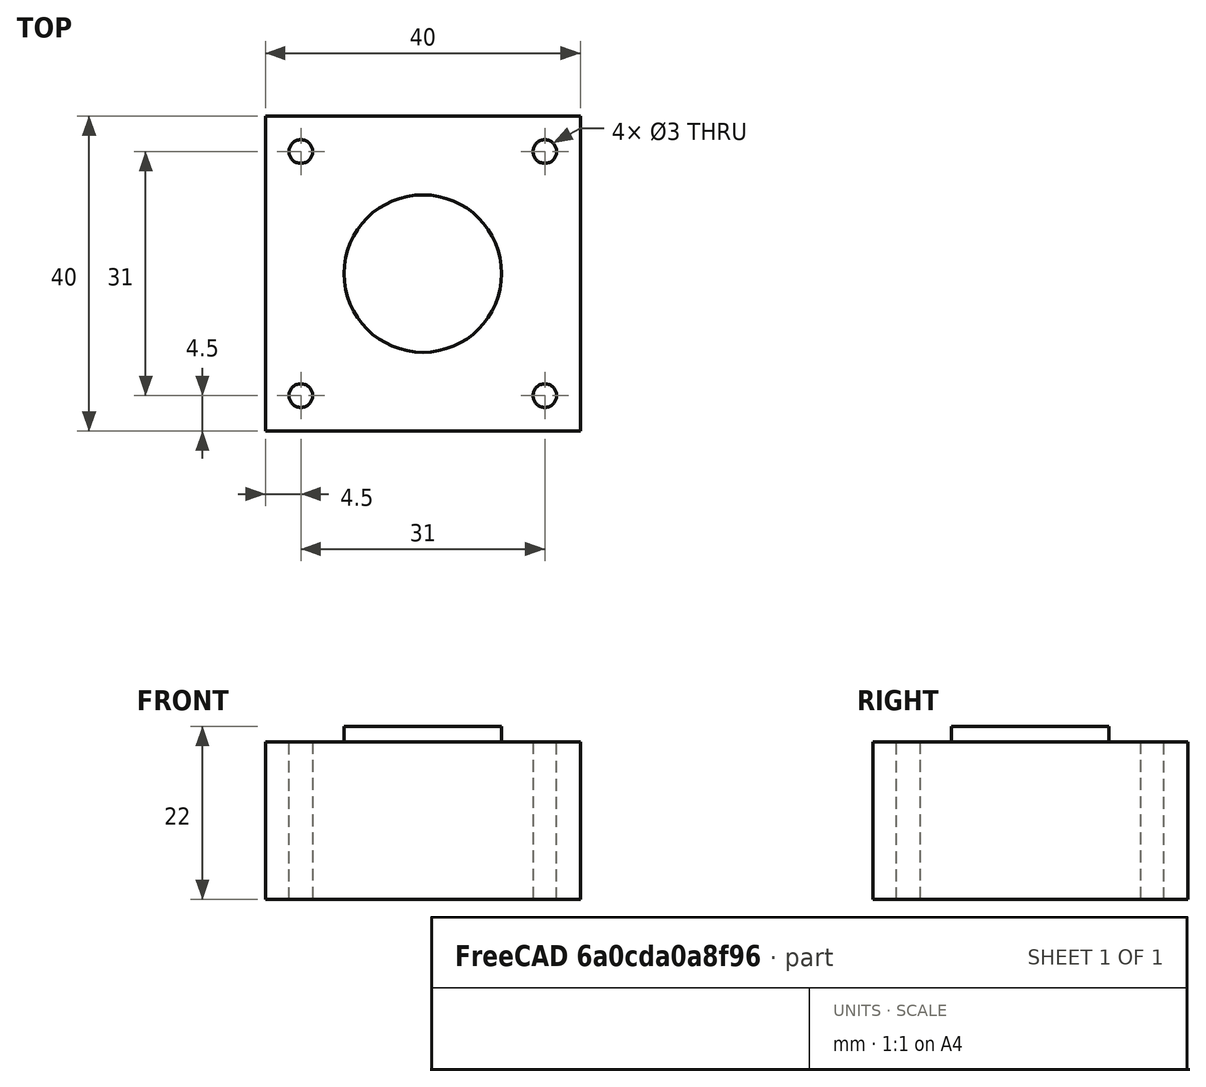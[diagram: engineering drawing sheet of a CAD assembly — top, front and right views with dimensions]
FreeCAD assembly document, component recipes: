
FREECAD ASSEMBLY — COMPONENT RECIPES ("Stepper")

This assembly document has 2 components, labeled P0..P1 below (a component is one placed body or linked part). 2 of them carry a construction recipe — the FreeCAD feature program that regenerates the part from scratch, quoted from this document or its linked companion documents; the rest are supplied as boundary geometry only. No exploded tour is included for this assembly.
COMPONENT P0 — recipe-attached ("Nema42_20", modeled in this document).
Construction recipe (the document's own serialized feature program — sketch geometry with constraints, then the solid features built on it; lengths are millimeters unless a unit is written):

FEATURE [Sketcher::SketchObject] Sketch018
  ArcFitTolerance = 1e-06
  AttachmentSupport = -> [XY_Plane005]
  FullyConstrained = true
  MakeInternals = false
  MapMode = 5
  sketch-geometry (5):
    g0: LineSegment StartX=20 StartY=-20 StartZ=0 EndX=20 EndY=20 EndZ=0
    g1: LineSegment StartX=20 StartY=20 StartZ=0 EndX=-20 EndY=20 EndZ=0
    g2: LineSegment StartX=-20 StartY=20 StartZ=0 EndX=-20 EndY=-20 EndZ=0
    g3: LineSegment StartX=-20 StartY=-20 StartZ=0 EndX=20 EndY=-20 EndZ=0
    g4: GeomPoint [constr] X=0 Y=0 Z=0
  constraints (12):
    c: Coincident(g0,g1)
    c: Coincident(g1,g2)
    c: Coincident(g2,g3)
    c: Coincident(g3,g0)
    c: Vertical(g0)
    c: Vertical(g2)
    c: Horizontal(g1)
    c: Horizontal(g3)
    c: Symmetric(g2,g0,g4)
    c: Coincident(g4,g-1)
    c: Distance(g-1,g1) = 20
    c: Distance(g-2,g2) = 20
FEATURE [PartDesign::Pad] Pad010
  Direction = (0,0,1)
  Length = 20
  Length2 = 10
  Profile = -> Sketch018
  ReferenceAxis = -> Sketch018 [N_Axis]
  Refine = true
  Suppressed = false
  Type = 0
FEATURE [Sketcher::SketchObject] Sketch019
  ArcFitTolerance = 1e-06
  AttachmentSupport = -> [Pad010]
  FullyConstrained = true
  MakeInternals = false
  MapMode = 5
  Placement = pos=(0,0,20) rot=(0,0,1;0rad)
  sketch-geometry (1):
    g0: Circle CenterX=0 CenterY=0 CenterZ=0 NormalX=0 NormalY=0 NormalZ=1 AngleXU=0 Radius=10
  constraints (2):
    c: Coincident(g0,g-1)
    c: Diameter(g0) = 20
FEATURE [PartDesign::Pad] Pad011
  BaseFeature = -> Pad010
  Direction = (0,0,1)
  Length = 2
  Length2 = 10
  Profile = -> Sketch019
  ReferenceAxis = -> Sketch019 [N_Axis]
  Refine = true
  Suppressed = false
  Type = 0
FEATURE [Sketcher::SketchObject] Sketch020
  ArcFitTolerance = 1e-06
  AttachmentSupport = -> [Pad011]
  FullyConstrained = true
  MakeInternals = false
  MapMode = 5
  Placement = pos=(0,0,20) rot=(0,0,1;0rad)
  sketch-geometry (1):
    g0: Circle CenterX=-15.5 CenterY=15.5 CenterZ=0 NormalX=0 NormalY=0 NormalZ=1 AngleXU=0 Radius=1.5
  constraints (3):
    c: Distance(g0,g-2) = 15.5
    c: DistanceY(g-1,g0) = 15.5
    c: Diameter(g0) = 3
FEATURE [PartDesign::Pocket] Pocket007
  BaseFeature = -> Pad011
  Direction = (0,0,-1)
  Length = 5
  Length2 = 5
  Profile = -> Sketch020
  ReferenceAxis = -> Sketch020 [N_Axis]
  Refine = true
  Suppressed = false
  Type = 1
FEATURE [PartDesign::PolarPattern] PolarPattern002
  Angle = 360
  Axis = -> Sketch020 [N_Axis]
  BaseFeature = -> Pocket007
  Mode = 0
  Occurrences = 4
  Offset = 120
  Originals = -> [Pocket007]
  Refine = true
  Suppressed = false
  TransformMode = 0
FEATURE [PartDesign::Body] Body005  label="Nema42_20"
  AllowCompound = false
  Group = -> [Sketch018,Pad010,Sketch019,Pad011,Sketch020,Pocket007,PolarPattern002]
  Origin = -> Origin005
  Placement = pos=(0,0,0) rot=(0,0,1;4.71239rad)
  Tip = -> PolarPattern002
COMPONENT P1 — recipe-attached ("GT2_Second_Min", a linked part whose construction recipe lives in a companion FreeCAD document of the same project; that document's serialized recipe follows).
Construction recipe (the companion document, serialized — sketch geometry with constraints, then the solid features built on it; lengths are millimeters unless a unit is written):

FCSTD DOCUMENT  (FreeCAD 1.0R39319 (Git))
Label: GT2_20
License: All rights reserved
LicenseURL: https://en.wikipedia.org/wiki/All_rights_reserved
objects: Sketcher::SketchObject×3, PartDesign::Pad×3, PartDesign::Body×1
note: 16 computed .brp shape members not serialized (recipe doc carries the construction recipe); baked Part::Feature solids carry a one-line shape summary decoded from their .brp

FEATURE [Sketcher::SketchObject] SketchGear
  ArcFitTolerance = 1e-06
  FullyConstrained = false
  MakeInternals = false
  MapMode = 5
  Placement = pos=(0,0,7.5) rot=(0,0,1;0rad)
  sketch-geometry (121):
    g0: ArcOfCircle CenterX=5.9622 CenterY=-0.75 CenterZ=0 NormalX=0 NormalY=0 NormalZ=1 AngleXU=8.1e-15 Radius=0.15 StartAngle=0 EndAngle=1.5708
    g1: ArcOfCircle CenterX=6.30816 CenterY=0.82798 CenterZ=0 NormalX=0 NormalY=0 NormalZ=-1 AngleXU=-1.3331 Radius=1.46929 StartAngle=0 EndAngle=0.255762
    g2: ArcOfCircle CenterX=5.92156 CenterY=0 CenterZ=0 NormalX=0 NormalY=0 NormalZ=-1 AngleXU=-0.984764 Radius=0.559359 StartAngle=0 EndAngle=1.96953
    g3: ArcOfCircle CenterX=6.30816 CenterY=-0.82798 CenterZ=0 NormalX=0 NormalY=0 NormalZ=-1 AngleXU=1.07734 Radius=1.46929 StartAngle=0 EndAngle=0.255762
    g4: ArcOfCircle CenterX=5.9622 CenterY=0.75 CenterZ=0 NormalX=0 NormalY=0 NormalZ=1 AngleXU=-1.5708 Radius=0.15 StartAngle=0 EndAngle=1.5708
    g5: LineSegment StartX=6.1122 StartY=0.75 StartZ=0 EndX=6.04481 EndY=1.17548 EndZ=0
    g6: ArcOfCircle CenterX=5.90215 CenterY=1.12913 CenterZ=0 NormalX=0 NormalY=0 NormalZ=1 AngleXU=0.314159 Radius=0.15 StartAngle=0 EndAngle=1.5708
    g7: ArcOfCircle CenterX=5.74356 CenterY=2.73679 CenterZ=0 NormalX=0 NormalY=0 NormalZ=-1 AngleXU=-1.64726 Radius=1.46929 StartAngle=0 EndAngle=0.255762
    g8: ArcOfCircle CenterX=5.63174 CenterY=1.82986 CenterZ=0 NormalX=0 NormalY=0 NormalZ=-1 AngleXU=-1.29892 Radius=0.559359 StartAngle=0 EndAngle=1.96953
    g9: ArcOfCircle CenterX=6.25528 CenterY=1.16187 CenterZ=0 NormalX=0 NormalY=0 NormalZ=-1 AngleXU=0.763178 Radius=1.46929 StartAngle=0 EndAngle=0.255762
    g10: ArcOfCircle CenterX=5.43862 CenterY=2.55571 CenterZ=0 NormalX=0 NormalY=0 NormalZ=1 AngleXU=-1.25664 Radius=0.15 StartAngle=0 EndAngle=1.5708
    g11: LineSegment StartX=5.58128 StartY=2.60207 StartZ=0 EndX=5.38571 EndY=2.9859 EndZ=0
    g12: ArcOfCircle CenterX=5.26436 CenterY=2.89773 CenterZ=0 NormalX=0 NormalY=0 NormalZ=1 AngleXU=0.628319 Radius=0.15 StartAngle=0 EndAngle=1.5708
    g13: ArcOfCircle CenterX=4.61674 CenterY=4.3777 CenterZ=0 NormalX=0 NormalY=0 NormalZ=-1 AngleXU=-1.96142 Radius=1.46929 StartAngle=0 EndAngle=0.255762
    g14: ArcOfCircle CenterX=4.79064 CenterY=3.4806 CenterZ=0 NormalX=0 NormalY=0 NormalZ=-1 AngleXU=-1.61308 Radius=0.559359 StartAngle=0 EndAngle=1.96953
    g15: ArcOfCircle CenterX=5.59009 CenterY=3.038 CenterZ=0 NormalX=0 NormalY=0 NormalZ=-1 AngleXU=0.449019 Radius=1.46929 StartAngle=0 EndAngle=0.255762
    g16: ArcOfCircle CenterX=4.38268 CenterY=4.11125 CenterZ=0 NormalX=0 NormalY=0 NormalZ=1 AngleXU=-0.942478 Radius=0.15 StartAngle=0 EndAngle=1.5708
    g17: LineSegment StartX=4.50403 StartY=4.19942 StartZ=0 EndX=4.19942 EndY=4.50403 EndZ=0
    g18: ArcOfCircle CenterX=4.11125 CenterY=4.38268 CenterZ=0 NormalX=0 NormalY=0 NormalZ=1 AngleXU=0.942478 Radius=0.15 StartAngle=0 EndAngle=1.5708
    g19: ArcOfCircle CenterX=3.038 CenterY=5.59009 CenterZ=0 NormalX=0 NormalY=0 NormalZ=-1 AngleXU=-2.27558 Radius=1.46929 StartAngle=0 EndAngle=0.255762
    g20: ArcOfCircle CenterX=3.4806 CenterY=4.79064 CenterZ=0 NormalX=0 NormalY=0 NormalZ=-1 AngleXU=-1.92724 Radius=0.559359 StartAngle=0 EndAngle=1.96953
    g21: ArcOfCircle CenterX=4.3777 CenterY=4.61674 CenterZ=0 NormalX=0 NormalY=0 NormalZ=-1 AngleXU=0.13486 Radius=1.46929 StartAngle=0 EndAngle=0.255762
    g22: ArcOfCircle CenterX=2.89773 CenterY=5.26436 CenterZ=0 NormalX=0 NormalY=0 NormalZ=1 AngleXU=-0.628319 Radius=0.15 StartAngle=0 EndAngle=1.5708
    g23: LineSegment StartX=2.9859 StartY=5.38571 StartZ=0 EndX=2.60207 EndY=5.58128 EndZ=0
    g24: ArcOfCircle CenterX=2.55571 CenterY=5.43862 CenterZ=0 NormalX=0 NormalY=0 NormalZ=1 AngleXU=1.25664 Radius=0.15 StartAngle=0 EndAngle=1.5708
    g25: ArcOfCircle CenterX=1.16187 CenterY=6.25528 CenterZ=0 NormalX=0 NormalY=0 NormalZ=-1 AngleXU=-2.58974 Radius=1.46929 StartAngle=0 EndAngle=0.255762
    g26: ArcOfCircle CenterX=1.82986 CenterY=5.63174 CenterZ=0 NormalX=0 NormalY=0 NormalZ=-1 AngleXU=-2.2414 Radius=0.559359 StartAngle=0 EndAngle=1.96953
    g27: ArcOfCircle CenterX=2.73679 CenterY=5.74356 CenterZ=0 NormalX=0 NormalY=0 NormalZ=-1 AngleXU=-0.1793 Radius=1.46929 StartAngle=0 EndAngle=0.255762
    g28: ArcOfCircle CenterX=1.12913 CenterY=5.90215 CenterZ=0 NormalX=0 NormalY=0 NormalZ=1 AngleXU=-0.314159 Radius=0.15 StartAngle=0 EndAngle=1.5708
    g29: LineSegment StartX=1.17548 StartY=6.04481 StartZ=0 EndX=0.75 EndY=6.1122 EndZ=0
    g30: ArcOfCircle CenterX=0.75 CenterY=5.9622 CenterZ=0 NormalX=0 NormalY=0 NormalZ=1 AngleXU=1.5708 Radius=0.15 StartAngle=0 EndAngle=1.5708
    g31: ArcOfCircle CenterX=-0.82798 CenterY=6.30816 CenterZ=0 NormalX=0 NormalY=0 NormalZ=-1 AngleXU=-2.9039 Radius=1.46929 StartAngle=0 EndAngle=0.255762
    g32: ArcOfCircle CenterX=4e-16 CenterY=5.92156 CenterZ=0 NormalX=0 NormalY=0 NormalZ=-1 AngleXU=-2.55556 Radius=0.559359 StartAngle=0 EndAngle=1.96953
    g33: ArcOfCircle CenterX=0.82798 CenterY=6.30816 CenterZ=0 NormalX=0 NormalY=0 NormalZ=-1 AngleXU=-0.493459 Radius=1.46929 StartAngle=0 EndAngle=0.255762
    g34: ArcOfCircle CenterX=-0.75 CenterY=5.9622 CenterZ=0 NormalX=0 NormalY=0 NormalZ=1 AngleXU=5.9e-15 Radius=0.15 StartAngle=0 EndAngle=1.5708
    g35: LineSegment StartX=-0.75 StartY=6.1122 StartZ=0 EndX=-1.17548 EndY=6.04481 EndZ=0
    g36: ArcOfCircle CenterX=-1.12913 CenterY=5.90215 CenterZ=0 NormalX=0 NormalY=0 NormalZ=1 AngleXU=1.88496 Radius=0.15 StartAngle=0 EndAngle=1.5708
    g37: ArcOfCircle CenterX=-2.73679 CenterY=5.74356 CenterZ=0 NormalX=0 NormalY=0 NormalZ=-1 AngleXU=3.06513 Radius=1.46929 StartAngle=0 EndAngle=0.255762
    g38: ArcOfCircle CenterX=-1.82986 CenterY=5.63174 CenterZ=0 NormalX=0 NormalY=0 NormalZ=-1 AngleXU=-2.86972 Radius=0.559359 StartAngle=0 EndAngle=1.96953
    g39: ArcOfCircle CenterX=-1.16187 CenterY=6.25528 CenterZ=0 NormalX=0 NormalY=0 NormalZ=-1 AngleXU=-0.807618 Radius=1.46929 StartAngle=0 EndAngle=0.255762
    g40: ArcOfCircle CenterX=-2.55571 CenterY=5.43862 CenterZ=0 NormalX=0 NormalY=0 NormalZ=1 AngleXU=0.314159 Radius=0.15 StartAngle=0 EndAngle=1.5708
    g41: LineSegment StartX=-2.60207 StartY=5.58128 StartZ=0 EndX=-2.9859 EndY=5.38571 EndZ=0
    g42: ArcOfCircle CenterX=-2.89773 CenterY=5.26436 CenterZ=0 NormalX=0 NormalY=0 NormalZ=1 AngleXU=2.19911 Radius=0.15 StartAngle=0 EndAngle=1.5708
    g43: ArcOfCircle CenterX=-4.3777 CenterY=4.61674 CenterZ=0 NormalX=0 NormalY=0 NormalZ=-1 AngleXU=2.75097 Radius=1.46929 StartAngle=0 EndAngle=0.255762
    g44: ArcOfCircle CenterX=-3.4806 CenterY=4.79064 CenterZ=0 NormalX=0 NormalY=0 NormalZ=-1 AngleXU=3.09931 Radius=0.559359 StartAngle=0 EndAngle=1.96953
    g45: ArcOfCircle CenterX=-3.038 CenterY=5.59009 CenterZ=0 NormalX=0 NormalY=0 NormalZ=-1 AngleXU=-1.12178 Radius=1.46929 StartAngle=0 EndAngle=0.255762
    g46: ArcOfCircle CenterX=-4.11125 CenterY=4.38268 CenterZ=0 NormalX=0 NormalY=0 NormalZ=1 AngleXU=0.628319 Radius=0.15 StartAngle=0 EndAngle=1.5708
    g47: LineSegment StartX=-4.19942 StartY=4.50403 StartZ=0 EndX=-4.50403 EndY=4.19942 EndZ=0
    g48: ArcOfCircle CenterX=-4.38268 CenterY=4.11125 CenterZ=0 NormalX=0 NormalY=0 NormalZ=1 AngleXU=2.51327 Radius=0.15 StartAngle=0 EndAngle=1.5708
    g49: ArcOfCircle CenterX=-5.59009 CenterY=3.038 CenterZ=0 NormalX=0 NormalY=0 NormalZ=-1 AngleXU=2.43681 Radius=1.46929 StartAngle=0 EndAngle=0.255762
    g50: ArcOfCircle CenterX=-4.79064 CenterY=3.4806 CenterZ=0 NormalX=0 NormalY=0 NormalZ=-1 AngleXU=2.78515 Radius=0.559359 StartAngle=0 EndAngle=1.96953
    g51: ArcOfCircle CenterX=-4.61674 CenterY=4.3777 CenterZ=0 NormalX=0 NormalY=0 NormalZ=-1 AngleXU=-1.43594 Radius=1.46929 StartAngle=0 EndAngle=0.255762
    g52: ArcOfCircle CenterX=-5.26436 CenterY=2.89773 CenterZ=0 NormalX=0 NormalY=0 NormalZ=1 AngleXU=0.942478 Radius=0.15 StartAngle=0 EndAngle=1.5708
    g53: LineSegment StartX=-5.38571 StartY=2.9859 StartZ=0 EndX=-5.58128 EndY=2.60207 EndZ=0
    g54: ArcOfCircle CenterX=-5.43862 CenterY=2.55571 CenterZ=0 NormalX=0 NormalY=0 NormalZ=1 AngleXU=2.82743 Radius=0.15 StartAngle=0 EndAngle=1.5708
    g55: ArcOfCircle CenterX=-6.25528 CenterY=1.16187 CenterZ=0 NormalX=0 NormalY=0 NormalZ=-1 AngleXU=2.12265 Radius=1.46929 StartAngle=0 EndAngle=0.255762
    g56: ArcOfCircle CenterX=-5.63174 CenterY=1.82986 CenterZ=0 NormalX=0 NormalY=0 NormalZ=-1 AngleXU=2.47099 Radius=0.559359 StartAngle=0 EndAngle=1.96953
    g57: ArcOfCircle CenterX=-5.74356 CenterY=2.73679 CenterZ=0 NormalX=0 NormalY=0 NormalZ=-1 AngleXU=-1.7501 Radius=1.46929 StartAngle=0 EndAngle=0.255762
    g58: ArcOfCircle CenterX=-5.90215 CenterY=1.12913 CenterZ=0 NormalX=0 NormalY=0 NormalZ=1 AngleXU=1.25664 Radius=0.15 StartAngle=0 EndAngle=1.5708
    g59: LineSegment StartX=-6.04481 StartY=1.17548 StartZ=0 EndX=-6.1122 EndY=0.75 EndZ=0
    g60: ArcOfCircle CenterX=-5.9622 CenterY=0.75 CenterZ=0 NormalX=0 NormalY=0 NormalZ=1 AngleXU=-3.14159 Radius=0.15 StartAngle=0 EndAngle=1.5708
    g61: ArcOfCircle CenterX=-6.30816 CenterY=-0.82798 CenterZ=0 NormalX=0 NormalY=0 NormalZ=-1 AngleXU=1.80849 Radius=1.46929 StartAngle=0 EndAngle=0.255762
    g62: ArcOfCircle CenterX=-5.92156 CenterY=9e-16 CenterZ=0 NormalX=0 NormalY=0 NormalZ=-1 AngleXU=2.15683 Radius=0.559359 StartAngle=0 EndAngle=1.96953
    g63: ArcOfCircle CenterX=-6.30816 CenterY=0.82798 CenterZ=0 NormalX=0 NormalY=0 NormalZ=-1 AngleXU=-2.06426 Radius=1.46929 StartAngle=0 EndAngle=0.255762
    g64: ArcOfCircle CenterX=-5.9622 CenterY=-0.75 CenterZ=0 NormalX=0 NormalY=0 NormalZ=1 AngleXU=1.5708 Radius=0.15 StartAngle=0 EndAngle=1.5708
    g65: LineSegment StartX=-6.1122 StartY=-0.75 StartZ=0 EndX=-6.04481 EndY=-1.17548 EndZ=0
    g66: ArcOfCircle CenterX=-5.90215 CenterY=-1.12913 CenterZ=0 NormalX=0 NormalY=0 NormalZ=1 AngleXU=-2.82743 Radius=0.15 StartAngle=0 EndAngle=1.5708
    g67: ArcOfCircle CenterX=-5.74356 CenterY=-2.73679 CenterZ=0 NormalX=0 NormalY=0 NormalZ=-1 AngleXU=1.49433 Radius=1.46929 StartAngle=0 EndAngle=0.255762
    g68: ArcOfCircle CenterX=-5.63174 CenterY=-1.82986 CenterZ=0 NormalX=0 NormalY=0 NormalZ=-1 AngleXU=1.84267 Radius=0.559359 StartAngle=0 EndAngle=1.96953
    g69: ArcOfCircle CenterX=-6.25528 CenterY=-1.16187 CenterZ=0 NormalX=0 NormalY=0 NormalZ=-1 AngleXU=-2.37841 Radius=1.46929 StartAngle=0 EndAngle=0.255762
    g70: ArcOfCircle CenterX=-5.43862 CenterY=-2.55571 CenterZ=0 NormalX=0 NormalY=0 NormalZ=1 AngleXU=1.88496 Radius=0.15 StartAngle=0 EndAngle=1.5708
    g71: LineSegment StartX=-5.58128 StartY=-2.60207 StartZ=0 EndX=-5.38571 EndY=-2.9859 EndZ=0
    g72: ArcOfCircle CenterX=-5.26436 CenterY=-2.89773 CenterZ=0 NormalX=0 NormalY=0 NormalZ=1 AngleXU=-2.51327 Radius=0.15 StartAngle=0 EndAngle=1.5708
    g73: ArcOfCircle CenterX=-4.61674 CenterY=-4.3777 CenterZ=0 NormalX=0 NormalY=0 NormalZ=-1 AngleXU=1.18017 Radius=1.46929 StartAngle=0 EndAngle=0.255762
    g74: ArcOfCircle CenterX=-4.79064 CenterY=-3.4806 CenterZ=0 NormalX=0 NormalY=0 NormalZ=-1 AngleXU=1.52851 Radius=0.559359 StartAngle=0 EndAngle=1.96953
    g75: ArcOfCircle CenterX=-5.59009 CenterY=-3.038 CenterZ=0 NormalX=0 NormalY=0 NormalZ=-1 AngleXU=-2.69257 Radius=1.46929 StartAngle=0 EndAngle=0.255762
    g76: ArcOfCircle CenterX=-4.38268 CenterY=-4.11125 CenterZ=0 NormalX=0 NormalY=0 NormalZ=1 AngleXU=2.19911 Radius=0.15 StartAngle=0 EndAngle=1.5708
    g77: LineSegment StartX=-4.50403 StartY=-4.19942 StartZ=0 EndX=-4.19942 EndY=-4.50403 EndZ=0
    g78: ArcOfCircle CenterX=-4.11125 CenterY=-4.38268 CenterZ=0 NormalX=0 NormalY=0 NormalZ=1 AngleXU=-2.19911 Radius=0.15 StartAngle=0 EndAngle=1.5708
    g79: ArcOfCircle CenterX=-3.038 CenterY=-5.59009 CenterZ=0 NormalX=0 NormalY=0 NormalZ=-1 AngleXU=0.866016 Radius=1.46929 StartAngle=0 EndAngle=0.255762
    g80: ArcOfCircle CenterX=-3.4806 CenterY=-4.79064 CenterZ=0 NormalX=0 NormalY=0 NormalZ=-1 AngleXU=1.21435 Radius=0.559359 StartAngle=0 EndAngle=1.96953
    g81: ArcOfCircle CenterX=-4.3777 CenterY=-4.61674 CenterZ=0 NormalX=0 NormalY=0 NormalZ=-1 AngleXU=-3.00673 Radius=1.46929 StartAngle=0 EndAngle=0.255762
    g82: ArcOfCircle CenterX=-2.89773 CenterY=-5.26436 CenterZ=0 NormalX=0 NormalY=0 NormalZ=1 AngleXU=2.51327 Radius=0.15 StartAngle=0 EndAngle=1.5708
    g83: LineSegment StartX=-2.9859 StartY=-5.38571 StartZ=0 EndX=-2.60207 EndY=-5.58128 EndZ=0
    g84: ArcOfCircle CenterX=-2.55571 CenterY=-5.43862 CenterZ=0 NormalX=0 NormalY=0 NormalZ=1 AngleXU=-1.88496 Radius=0.15 StartAngle=0 EndAngle=1.5708
    g85: ArcOfCircle CenterX=-1.16187 CenterY=-6.25528 CenterZ=0 NormalX=0 NormalY=0 NormalZ=-1 AngleXU=0.551856 Radius=1.46929 StartAngle=0 EndAngle=0.255762
    g86: ArcOfCircle CenterX=-1.82986 CenterY=-5.63174 CenterZ=0 NormalX=0 NormalY=0 NormalZ=-1 AngleXU=0.900192 Radius=0.559359 StartAngle=0 EndAngle=1.96953
    g87: ArcOfCircle CenterX=-2.73679 CenterY=-5.74356 CenterZ=0 NormalX=0 NormalY=0 NormalZ=-1 AngleXU=2.96229 Radius=1.46929 StartAngle=0 EndAngle=0.255762
    g88: ArcOfCircle CenterX=-1.12913 CenterY=-5.90215 CenterZ=0 NormalX=0 NormalY=0 NormalZ=1 AngleXU=2.82743 Radius=0.15 StartAngle=0 EndAngle=1.5708
    g89: LineSegment StartX=-1.17548 StartY=-6.04481 StartZ=0 EndX=-0.75 EndY=-6.1122 EndZ=0
    g90: ArcOfCircle CenterX=-0.75 CenterY=-5.9622 CenterZ=0 NormalX=0 NormalY=0 NormalZ=1 AngleXU=-1.5708 Radius=0.15 StartAngle=0 EndAngle=1.5708
    g91: ArcOfCircle CenterX=0.82798 CenterY=-6.30816 CenterZ=0 NormalX=0 NormalY=0 NormalZ=-1 AngleXU=0.237697 Radius=1.46929 StartAngle=0 EndAngle=0.255762
    g92: ArcOfCircle CenterX=-9e-16 CenterY=-5.92156 CenterZ=0 NormalX=0 NormalY=0 NormalZ=-1 AngleXU=0.586033 Radius=0.559359 StartAngle=0 EndAngle=1.96953
    g93: ArcOfCircle CenterX=-0.82798 CenterY=-6.30816 CenterZ=0 NormalX=0 NormalY=0 NormalZ=-1 AngleXU=2.64813 Radius=1.46929 StartAngle=0 EndAngle=0.255762
    g94: ArcOfCircle CenterX=0.75 CenterY=-5.9622 CenterZ=0 NormalX=0 NormalY=0 NormalZ=1 AngleXU=-3.14159 Radius=0.15 StartAngle=0 EndAngle=1.5708
    g95: LineSegment StartX=0.75 StartY=-6.1122 StartZ=0 EndX=1.17548 EndY=-6.04481 EndZ=0
    g96: ArcOfCircle CenterX=1.12913 CenterY=-5.90215 CenterZ=0 NormalX=0 NormalY=0 NormalZ=1 AngleXU=-1.25664 Radius=0.15 StartAngle=0 EndAngle=1.5708
    g97: ArcOfCircle CenterX=2.73679 CenterY=-5.74356 CenterZ=0 NormalX=0 NormalY=0 NormalZ=-1 AngleXU=-0.0764622 Radius=1.46929 StartAngle=0 EndAngle=0.255762
    g98: ArcOfCircle CenterX=1.82986 CenterY=-5.63174 CenterZ=0 NormalX=0 NormalY=0 NormalZ=-1 AngleXU=0.271874 Radius=0.559359 StartAngle=0 EndAngle=1.96953
    g99: ArcOfCircle CenterX=1.16187 CenterY=-6.25528 CenterZ=0 NormalX=0 NormalY=0 NormalZ=-1 AngleXU=2.33397 Radius=1.46929 StartAngle=0 EndAngle=0.255762
    g100: ArcOfCircle CenterX=2.55571 CenterY=-5.43862 CenterZ=0 NormalX=0 NormalY=0 NormalZ=1 AngleXU=-2.82743 Radius=0.15 StartAngle=0 EndAngle=1.5708
    g101: LineSegment StartX=2.60207 StartY=-5.58128 StartZ=0 EndX=2.9859 EndY=-5.38571 EndZ=0
    g102: ArcOfCircle CenterX=2.89773 CenterY=-5.26436 CenterZ=0 NormalX=0 NormalY=0 NormalZ=1 AngleXU=-0.942478 Radius=0.15 StartAngle=0 EndAngle=1.5708
    g103: ArcOfCircle CenterX=4.3777 CenterY=-4.61674 CenterZ=0 NormalX=0 NormalY=0 NormalZ=-1 AngleXU=-0.390621 Radius=1.46929 StartAngle=0 EndAngle=0.255762
    g104: ArcOfCircle CenterX=3.4806 CenterY=-4.79064 CenterZ=0 NormalX=0 NormalY=0 NormalZ=-1 AngleXU=-0.0422858 Radius=0.559359 StartAngle=0 EndAngle=1.96953
    g105: ArcOfCircle CenterX=3.038 CenterY=-5.59009 CenterZ=0 NormalX=0 NormalY=0 NormalZ=-1 AngleXU=2.01982 Radius=1.46929 StartAngle=0 EndAngle=0.255762
    g106: ArcOfCircle CenterX=4.11125 CenterY=-4.38268 CenterZ=0 NormalX=0 NormalY=0 NormalZ=1 AngleXU=-2.51327 Radius=0.15 StartAngle=0 EndAngle=1.5708
    g107: LineSegment StartX=4.19942 StartY=-4.50403 StartZ=0 EndX=4.50403 EndY=-4.19942 EndZ=0
    g108: ArcOfCircle CenterX=4.38268 CenterY=-4.11125 CenterZ=0 NormalX=0 NormalY=0 NormalZ=1 AngleXU=-0.628319 Radius=0.15 StartAngle=0 EndAngle=1.5708
    g109: ArcOfCircle CenterX=5.59009 CenterY=-3.038 CenterZ=0 NormalX=0 NormalY=0 NormalZ=-1 AngleXU=-0.704781 Radius=1.46929 StartAngle=0 EndAngle=0.255762
    g110: ArcOfCircle CenterX=4.79064 CenterY=-3.4806 CenterZ=0 NormalX=0 NormalY=0 NormalZ=-1 AngleXU=-0.356445 Radius=0.559359 StartAngle=0 EndAngle=1.96953
    g111: ArcOfCircle CenterX=4.61674 CenterY=-4.3777 CenterZ=0 NormalX=0 NormalY=0 NormalZ=-1 AngleXU=1.70566 Radius=1.46929 StartAngle=0 EndAngle=0.255762
    g112: ArcOfCircle CenterX=5.26436 CenterY=-2.89773 CenterZ=0 NormalX=0 NormalY=0 NormalZ=1 AngleXU=-2.19911 Radius=0.15 StartAngle=0 EndAngle=1.5708
    g113: LineSegment StartX=5.38571 StartY=-2.9859 StartZ=0 EndX=5.58128 EndY=-2.60207 EndZ=0
    g114: ArcOfCircle CenterX=5.43862 CenterY=-2.55571 CenterZ=0 NormalX=0 NormalY=0 NormalZ=1 AngleXU=-0.314159 Radius=0.15 StartAngle=0 EndAngle=1.5708
    g115: ArcOfCircle CenterX=6.25528 CenterY=-1.16187 CenterZ=0 NormalX=0 NormalY=0 NormalZ=-1 AngleXU=-1.01894 Radius=1.46929 StartAngle=0 EndAngle=0.255762
    g116: ArcOfCircle CenterX=5.63174 CenterY=-1.82986 CenterZ=0 NormalX=0 NormalY=0 NormalZ=-1 AngleXU=-0.670604 Radius=0.559359 StartAngle=0 EndAngle=1.96953
    g117: ArcOfCircle CenterX=5.74356 CenterY=-2.73679 CenterZ=0 NormalX=0 NormalY=0 NormalZ=-1 AngleXU=1.3915 Radius=1.46929 StartAngle=0 EndAngle=0.255762
    g118: ArcOfCircle CenterX=5.90215 CenterY=-1.12913 CenterZ=0 NormalX=0 NormalY=0 NormalZ=1 AngleXU=-1.88496 Radius=0.15 StartAngle=0 EndAngle=1.5708
    g119: LineSegment StartX=6.04481 StartY=-1.17548 StartZ=0 EndX=6.1122 EndY=-0.75 EndZ=0
    g120: Circle CenterX=0 CenterY=0 CenterZ=0 NormalX=0 NormalY=0 NormalZ=1 AngleXU=0 Radius=2.5
FEATURE [PartDesign::Pad] Pad
  Direction = (0,0,1)
  Length = 7.5
  Length2 = 10
  Placement = pos=(0,0,7.5) rot=(0,0,1;0rad)
  Profile = -> SketchGear
  ReferenceAxis = -> SketchGear [N_Axis]
  Refine = true
  Suppressed = false
  Type = 0
FEATURE [Sketcher::SketchObject] SketchBase
  ArcFitTolerance = 1e-06
  AttachmentOffset = pos=(0,0,-1) rot=(0,0,1;0rad)
  FullyConstrained = false
  MakeInternals = false
  MapMode = 5
  sketch-geometry (2):
    g0: Circle CenterX=0 CenterY=0 CenterZ=0 NormalX=0 NormalY=0 NormalZ=1 AngleXU=0 Radius=8
    g1: Circle CenterX=0 CenterY=0 CenterZ=0 NormalX=0 NormalY=0 NormalZ=1 AngleXU=0 Radius=2.5
  constraints (1):
    c: Diameter(g0) = 16
FEATURE [PartDesign::Pad] PadBase
  BaseFeature = -> Pad
  Direction = (0,0,1)
  Length = 7.5
  Length2 = 10
  Placement = pos=(0,0,7.5) rot=(0,0,1;0rad)
  Profile = -> SketchBase
  ReferenceAxis = -> SketchBase [N_Axis]
  Refine = true
  Suppressed = false
  Type = 0
FEATURE [Sketcher::SketchObject] SketchTop
  ArcFitTolerance = 1e-06
  AttachmentOffset = pos=(0,0,16) rot=(0,0,1;0rad)
  FullyConstrained = false
  MakeInternals = false
  MapMode = 5
  Placement = pos=(0,0,15) rot=(0,0,1;0rad)
  sketch-geometry (2):
    g0: Circle CenterX=0 CenterY=0 CenterZ=0 NormalX=0 NormalY=0 NormalZ=1 AngleXU=0 Radius=8
    g1: Circle CenterX=0 CenterY=0 CenterZ=0 NormalX=0 NormalY=0 NormalZ=1 AngleXU=0 Radius=2.5
  constraints (1):
    c: Diameter(g0) = 16
FEATURE [PartDesign::Pad] PadTop
  BaseFeature = -> PadBase
  Direction = (0,0,1)
  Length = 1
  Length2 = 10
  Placement = pos=(0,0,7.5) rot=(0,0,1;0rad)
  Profile = -> SketchTop
  ReferenceAxis = -> SketchTop [N_Axis]
  Refine = true
  Suppressed = false
  Type = 0
FEATURE [PartDesign::Body] Gear  label="GT2_Second_Min"
  AllowCompound = false
  Group = -> [SketchGear,Pad,SketchBase,PadBase,SketchTop,PadTop]
  Origin = -> Origin
  Tip = -> PadTop
PROVENANCE & LICENSES
A FreeCAD (.FCStd) document from a public repository crawl; recipes are the document's own serialized feature recipes (and, for linked parts, companion documents' recipes).
License: as declared in the source repository (recorded in the dataset sidecar).
